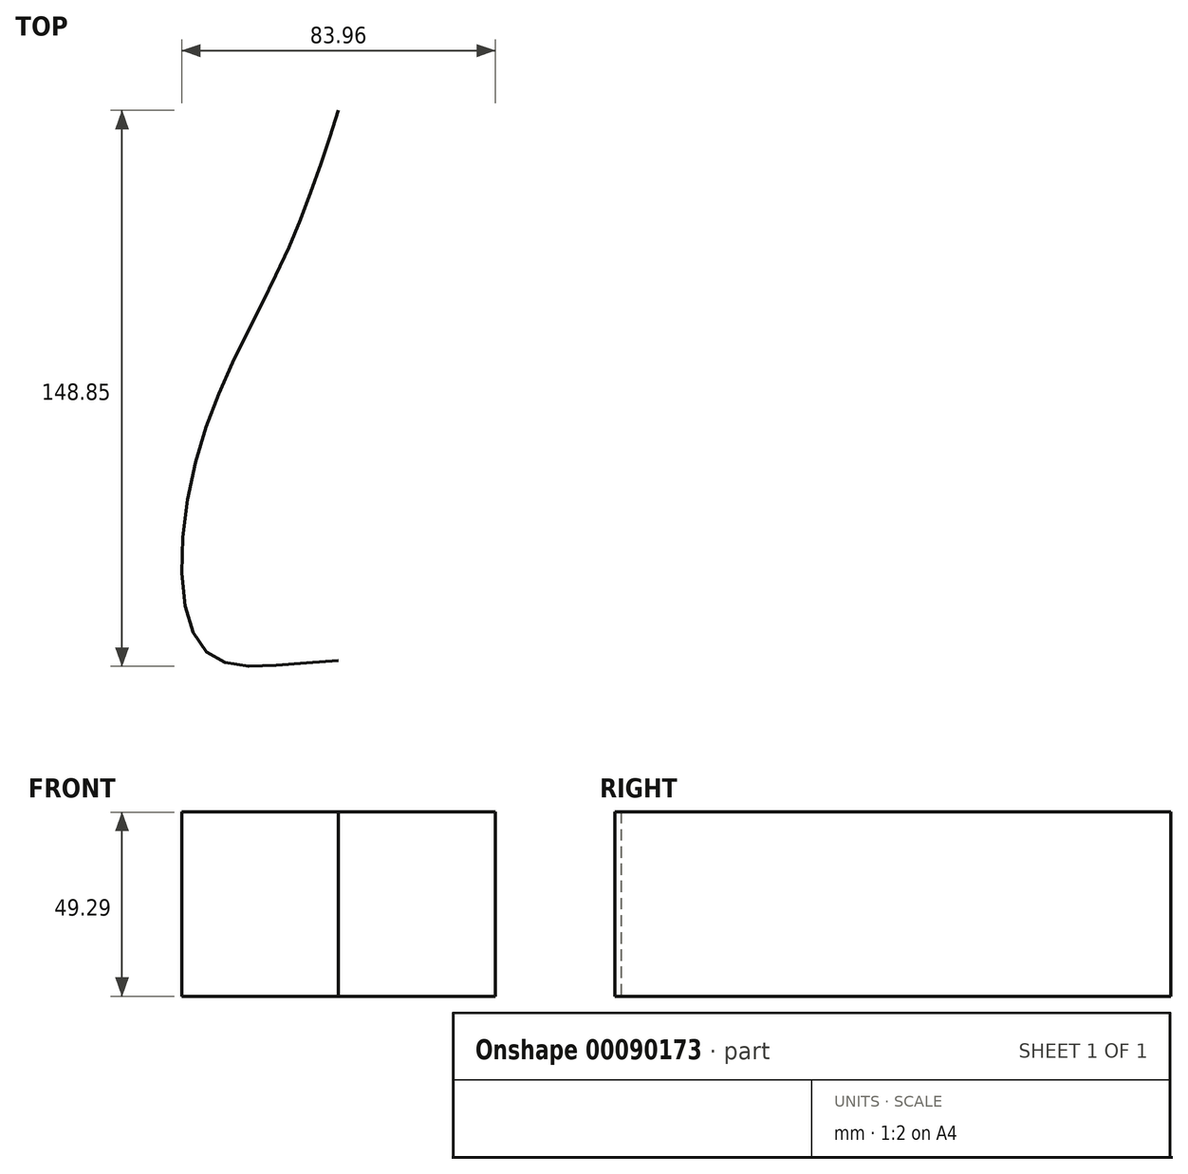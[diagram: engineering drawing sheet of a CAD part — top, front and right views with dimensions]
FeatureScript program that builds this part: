
annotation { "Feature Type Name" : "Feature", "Feature Type Description" : "" }
export const myFeature = defineFeature(function(context is Context, id is Id, definition is map)
    precondition{}
    {
        {
            var Q0;
            Q0=qCreatedBy(makeId("Top.planeOp"),FACE);
            var sketch = newSketch(context, id + "F0", { "sketchPlane" : qUnion([Q0])});
            skFitSpline(sketch, "E0", {"points": [v(0, -44.6) * mm, v(35.53, -42.28) * mm, v(38.16, 8.83) * mm, v(15.21, 61.7) * mm, v(0, 102.63) * mm], "startDerivative": vector(201.61, -7.31) * mm, "endDerivative": vector(-53.03, 164.48) * mm});
            skFitSpline(sketch, "E1.MirrorCS", {"points": [v(0, -44.6) * mm, v(-35.53, -42.28) * mm, v(-38.16, 8.83) * mm, v(-15.21, 61.7) * mm, v(0, 102.63) * mm], "startDerivative": vector(-201.61, -7.31) * mm, "endDerivative": vector(53.03, 164.48) * mm});
            skSolve(sketch);
        }
        {
            var Q0;
            Q0=makeQuery(id+"F0.imprint","IMPRINT",FACE,{"disambiguationData":[TD([[makeQuery(id+"F0.imprint","IMPRINT",EDGE,{"derivedFrom":sQuery(id+"F0.wireOp",EDGE,"E0")}),1.0]])]});
            extrude(context, id + "F1", {"entities" : qUnion([Q0]), "depth" : 49.3 * mm});
        }
    });
